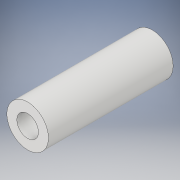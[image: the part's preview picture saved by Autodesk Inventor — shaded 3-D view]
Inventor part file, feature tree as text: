
AUTODESK INVENTOR PART (.ipt)
format: ipt  version: 2017 (Build 210142000, 142)  size: 96,768 bytes
history: native  units: in
note: dims shown in document units (in); Inventor stores cm internally (conversion verified against a paired STEP export)
features: extrude x1, sketch x1
ambient origin geometry x8: Origin, YZ Plane, XZ Plane, XY Plane, X Axis, Y Axis, Z Axis, Center Point
bodies: Solid1 (feature_tree)
feature tree (2):
  extrude  "Extrusion1"  Depth=1.5in
  sketch  "Sketch1"  dims[d0=0.26in d1=0.5in d2=1.5in d3=0.0in]
